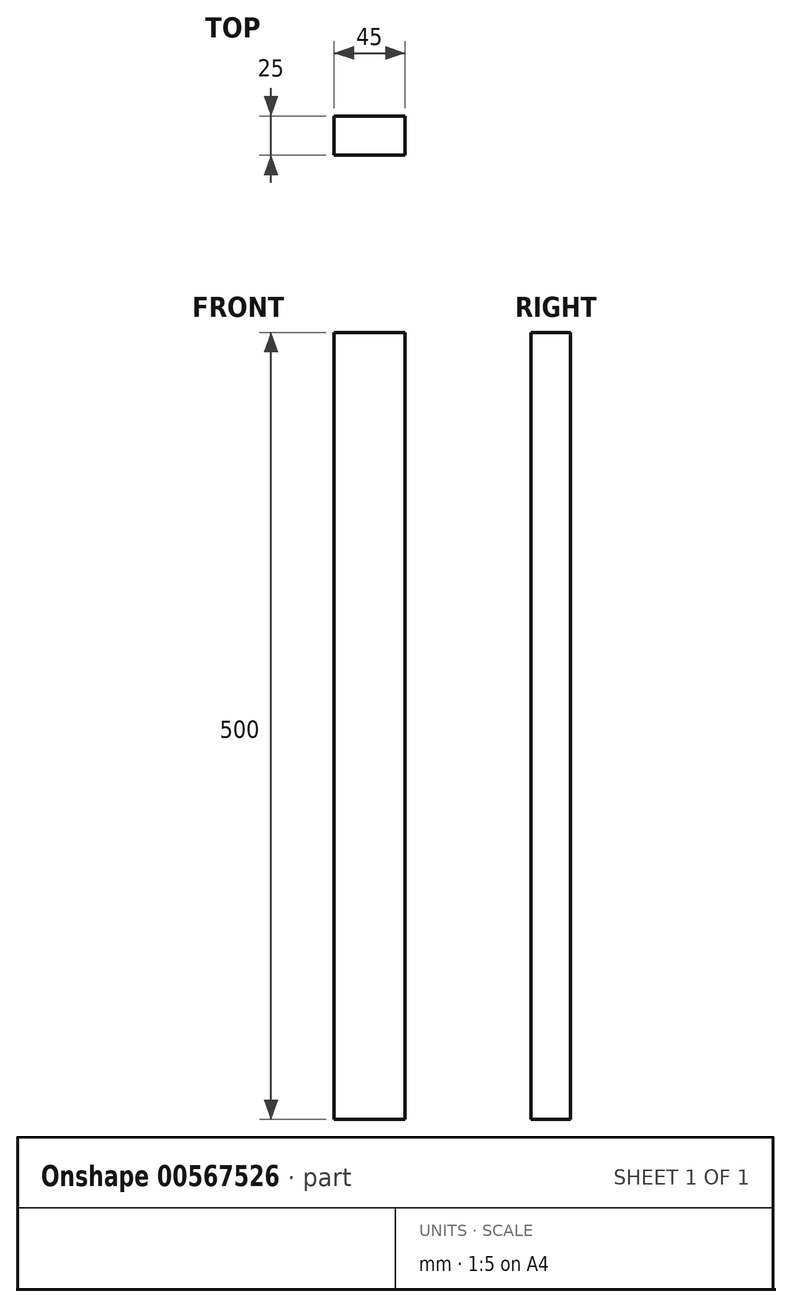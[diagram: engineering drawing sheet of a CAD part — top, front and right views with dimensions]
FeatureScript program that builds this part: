
annotation { "Feature Type Name" : "Feature", "Feature Type Description" : "" }
export const myFeature = defineFeature(function(context is Context, id is Id, definition is map)
    precondition{}
    {
        {
            var Q0;
            Q0=qCreatedBy(makeId("Front.planeOp"),FACE);
            var sketch = newSketch(context, id + "F0", { "sketchPlane" : qUnion([Q0])});
            skLineSegment(sketch, "E0.bottom", {"start": v(-75.26, 322.15) * mm, "end": v(-30.26, 322.15) * mm});
            skLineSegment(sketch, "E0.top", {"start": v(-75.26, -177.85) * mm, "end": v(-30.26, -177.85) * mm});
            skLineSegment(sketch, "E0.left", {"start": v(-75.26, 322.15) * mm, "end": v(-75.26, -177.85) * mm});
            skLineSegment(sketch, "E0.right", {"start": v(-30.26, 322.15) * mm, "end": v(-30.26, -177.85) * mm});
            skSolve(sketch);
        }
        {
            var Q0;
            Q0 = qSketchRegion(id + "F0", true);
            extrude(context, id + "F1", {"entities" : qUnion([Q0]), "depth" : 25 * mm, "offsetDistance" : 25 * mm});
        }
    });
